# Revit family: AC-C8T
name_source: partatom
category: Communication Devices
revit_build: Autodesk Revit 2014 (Build: 20130308_1515(x64)
units: mm (PartAtom-declared; Revit-internal decimal feet)

## types (1)
- AC-C8T
    100V Taps = 60, 30, 15, 7.5
    70V Taps = 60, 30, 15, 7.5, 3.8
    Coverage Horizontal = 100.00°
    Coverage Vertical = 100.00°
    Default Elevation = 0"
    Depth = 11.2599"
    Description = 8" Coaxial 2-way Loudspeaker Element
    Enclosure Depth = 6.9685"
    Enclosure Radius = 4.5866"
    Grille Depth = 0.5512"
    Grille Radius Base = 6.2205"
    Grille Radius Extent = 5.5"
    Impedance = 8
    Manufacturer = QSC Audio Products, LLC
    Manufacturer URL = www.qscaudio.com
    Middle Depth = 3.7402"
    Middle Radius = 5.0197"
    Model = AC-C8T
    Power Handling = 80
    Product Documentation Link = http://www.qsc.com
    Product Page URL = http://www.qsc.com
    Regulatory Compliance = UL1480, UL2043
    SPL Max = 114
    Sensitivity = 89
    URL = http://www.qscaudio.com
    Weight Dimensional (kg) = 13.3
    Weight Dimensional (lb) = 29.3
    Weight Product (kg) = 5.2
    Weight Product (lb) = 11.5
    Width = 12.441"

## geometry (parser evidence)
native form markers: Blend x11, Sweep x1
no freeform markers — native parametric forms only
